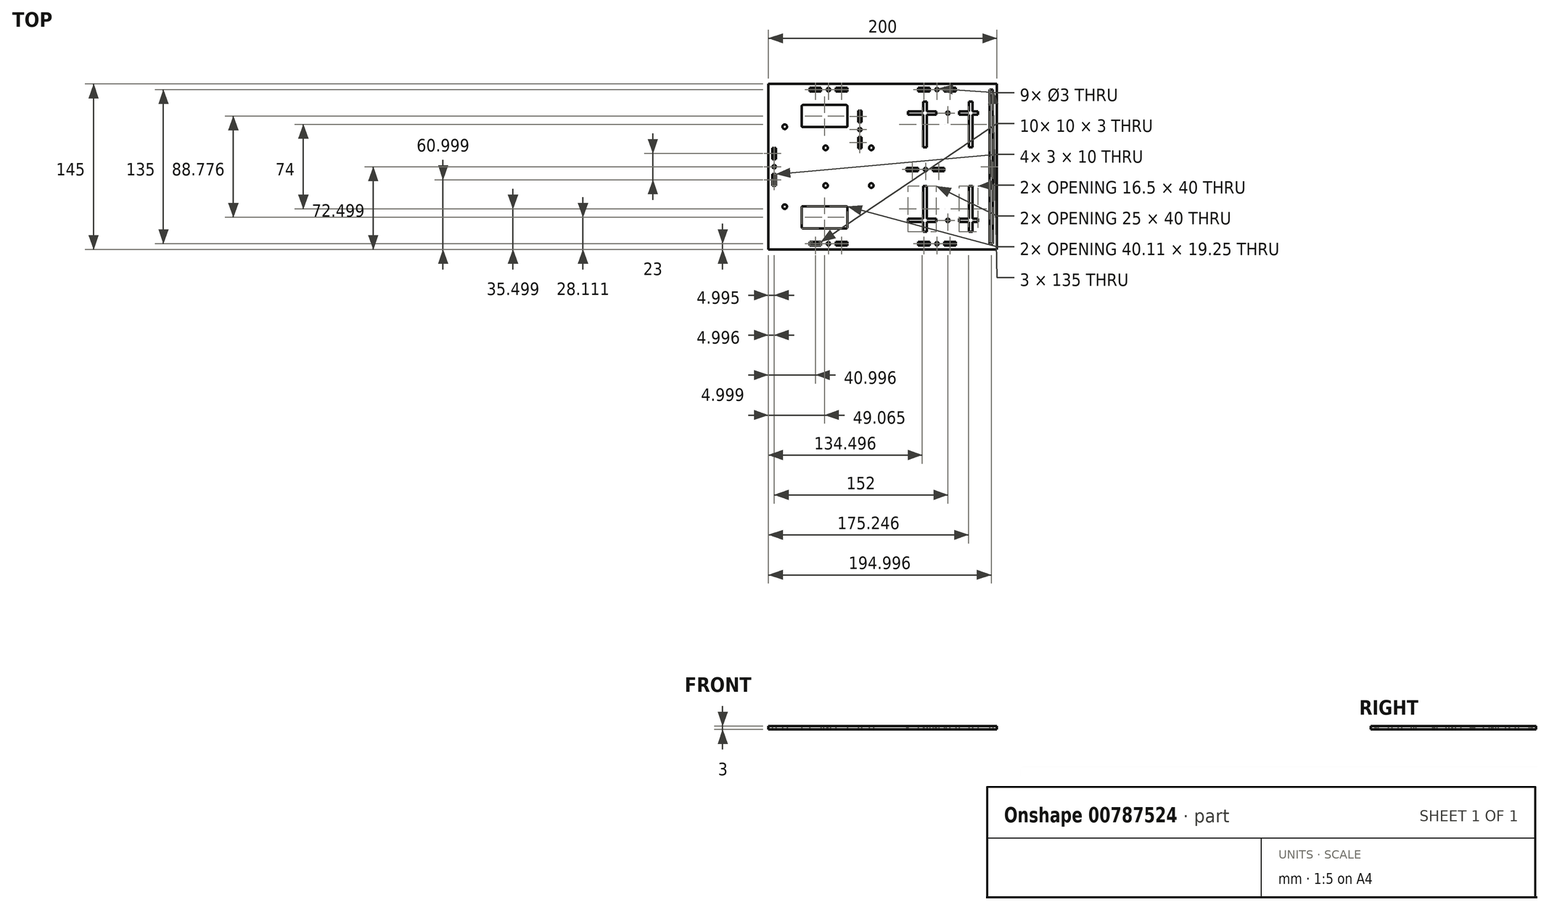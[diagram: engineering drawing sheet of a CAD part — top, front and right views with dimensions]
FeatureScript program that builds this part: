
annotation { "Feature Type Name" : "Feature", "Feature Type Description" : "" }
export const myFeature = defineFeature(function(context is Context, id is Id, definition is map)
    precondition{}
    {
        {
            var Q0;
            Q0=qCreatedBy(makeId("Top.planeOp"),FACE);
            var sketch = newSketch(context, id + "F0", { "sketchPlane" : qUnion([Q0])});
            skLineSegment(sketch, "E0.bottom", {"start": v(-57.36, 121.67) * mm, "end": v(142.64, 121.67) * mm});
            skLineSegment(sketch, "E0.top", {"start": v(-57.36, -23.33) * mm, "end": v(142.64, -23.33) * mm});
            skLineSegment(sketch, "E0.left", {"start": v(-57.36, 121.67) * mm, "end": v(-57.36, -23.33) * mm});
            skLineSegment(sketch, "E0.right", {"start": v(142.64, 121.67) * mm, "end": v(142.64, -23.33) * mm});
            skLineSegment(sketch, "E1.top", {"start": v(137.64, 46.67) * mm, "end": v(22.64, 46.67) * mm, "construction": true});
            skLineSegment(sketch, "E1.right", {"start": v(22.64, 116.67) * mm, "end": v(22.64, 46.67) * mm, "construction": true});
            skLineSegment(sketch, "E2", {"start": v(-57.36, 49.17) * mm, "end": v(-42.36, 49.17) * mm, "construction": true});
            skLineSegment(sketch, "E3.0", {"start": v(137.64, 116.67) * mm, "end": v(137.64, -18.33) * mm, "construction": true});
            skLineSegment(sketch, "E4.bottom", {"start": v(136.14, 116.67) * mm, "end": v(139.14, 116.67) * mm});
            skLineSegment(sketch, "E4.top", {"start": v(136.14, -18.33) * mm, "end": v(139.14, -18.33) * mm});
            skLineSegment(sketch, "E4.left", {"start": v(136.14, 116.67) * mm, "end": v(136.14, -18.33) * mm});
            skLineSegment(sketch, "E4.right", {"start": v(139.14, 116.67) * mm, "end": v(139.14, -18.33) * mm});
            skPoint(sketch, "E4.middle", {"position": v(137.64, 49.17) * mm});
            skLineSegment(sketch, "E5.0", {"start": v(-52.36, 116.67) * mm, "end": v(146, 116.67) * mm, "construction": true});
            skLineSegment(sketch, "E6.0", {"start": v(-52.36, 116.67) * mm, "end": v(-52.36, -18.33) * mm, "construction": true});
            skLineSegment(sketch, "E7.0", {"start": v(-52.36, -18.33) * mm, "end": v(139.14, -18.33) * mm, "construction": true});
            skCircle(sketch, "E8", {"center": v(90.14, 116.67) * mm, "radius": 1.5 * mm});
            skCircle(sketch, "E9", {"center": v(-4.86, 116.67) * mm, "radius": 1.5 * mm});
            skPoint(sketch, "E10", {"position": v(-52.36, 116.67) * mm});
            skLineSegment(sketch, "E11.bottom", {"start": v(-21.36, 118.17) * mm, "end": v(-11.36, 118.17) * mm});
            skLineSegment(sketch, "E11.top", {"start": v(-21.36, 115.17) * mm, "end": v(-11.36, 115.17) * mm});
            skLineSegment(sketch, "E11.left", {"start": v(-21.36, 118.17) * mm, "end": v(-21.36, 115.17) * mm});
            skLineSegment(sketch, "E11.right", {"start": v(-11.36, 118.17) * mm, "end": v(-11.36, 115.17) * mm});
            skPoint(sketch, "E11.middle", {"position": v(-16.36, 116.67) * mm});
            skLineSegment(sketch, "E12.bottom", {"start": v(1.64, 118.17) * mm, "end": v(11.64, 118.17) * mm});
            skLineSegment(sketch, "E12.top", {"start": v(1.64, 115.17) * mm, "end": v(11.64, 115.17) * mm});
            skLineSegment(sketch, "E12.left", {"start": v(1.64, 118.17) * mm, "end": v(1.64, 115.17) * mm});
            skLineSegment(sketch, "E12.right", {"start": v(11.64, 118.17) * mm, "end": v(11.64, 115.17) * mm});
            skPoint(sketch, "E12.middle", {"position": v(6.64, 116.67) * mm});
            skLineSegment(sketch, "E13.bottom", {"start": v(73.64, 118.17) * mm, "end": v(83.64, 118.17) * mm});
            skLineSegment(sketch, "E13.top", {"start": v(73.64, 115.17) * mm, "end": v(83.64, 115.17) * mm});
            skLineSegment(sketch, "E13.left", {"start": v(73.64, 118.17) * mm, "end": v(73.64, 115.17) * mm});
            skLineSegment(sketch, "E13.right", {"start": v(83.64, 118.17) * mm, "end": v(83.64, 115.17) * mm});
            skPoint(sketch, "E13.middle", {"position": v(78.64, 116.67) * mm});
            skLineSegment(sketch, "E14.bottom", {"start": v(96.64, 118.17) * mm, "end": v(106.64, 118.17) * mm});
            skLineSegment(sketch, "E14.top", {"start": v(96.64, 115.17) * mm, "end": v(106.64, 115.17) * mm});
            skLineSegment(sketch, "E14.left", {"start": v(96.64, 118.17) * mm, "end": v(96.64, 115.17) * mm});
            skLineSegment(sketch, "E14.right", {"start": v(106.64, 118.17) * mm, "end": v(106.64, 115.17) * mm});
            skPoint(sketch, "E14.middle", {"position": v(101.64, 116.67) * mm});
            skLineSegment(sketch, "E15.MirrorCS", {"start": v(11.64, -19.83) * mm, "end": v(11.64, -16.83) * mm});
            skLineSegment(sketch, "E16.MirrorCS", {"start": v(-21.36, -19.83) * mm, "end": v(-11.36, -19.83) * mm});
            skLineSegment(sketch, "E17.MirrorCS", {"start": v(-21.36, -16.83) * mm, "end": v(-11.36, -16.83) * mm});
            skLineSegment(sketch, "E18.MirrorCS", {"start": v(1.64, -19.83) * mm, "end": v(11.64, -19.83) * mm});
            skLineSegment(sketch, "E19.MirrorCS", {"start": v(-21.36, -19.83) * mm, "end": v(-21.36, -16.83) * mm});
            skLineSegment(sketch, "E20.MirrorCS", {"start": v(1.64, -16.83) * mm, "end": v(11.64, -16.83) * mm});
            skCircle(sketch, "E21.MirrorC", {"center": v(-4.86, -18.33) * mm, "radius": 1.5 * mm});
            skPoint(sketch, "E22.MirrorP", {"position": v(-16.36, -18.33) * mm});
            skLineSegment(sketch, "E23.MirrorCS", {"start": v(-11.36, -19.83) * mm, "end": v(-11.36, -16.83) * mm});
            skLineSegment(sketch, "E24.MirrorCS", {"start": v(1.64, -19.83) * mm, "end": v(1.64, -16.83) * mm});
            skPoint(sketch, "E25.MirrorP", {"position": v(6.64, -18.33) * mm});
            skLineSegment(sketch, "E26.MirrorCS", {"start": v(106.64, -19.83) * mm, "end": v(106.64, -16.83) * mm});
            skLineSegment(sketch, "E27.MirrorCS", {"start": v(83.64, -19.83) * mm, "end": v(83.64, -16.83) * mm});
            skLineSegment(sketch, "E28.MirrorCS", {"start": v(96.64, -19.83) * mm, "end": v(96.64, -16.83) * mm});
            skLineSegment(sketch, "E29.MirrorCS", {"start": v(73.64, -19.83) * mm, "end": v(73.64, -16.83) * mm});
            skPoint(sketch, "E30.MirrorP", {"position": v(101.64, -18.33) * mm});
            skCircle(sketch, "E31.MirrorC", {"center": v(90.14, -18.33) * mm, "radius": 1.5 * mm});
            skLineSegment(sketch, "E32.MirrorCS", {"start": v(73.64, -16.83) * mm, "end": v(83.64, -16.83) * mm});
            skLineSegment(sketch, "E33.MirrorCS", {"start": v(96.64, -16.83) * mm, "end": v(106.64, -16.83) * mm});
            skPoint(sketch, "E34.MirrorP", {"position": v(78.64, -18.33) * mm});
            skLineSegment(sketch, "E35.MirrorCS", {"start": v(73.64, -19.83) * mm, "end": v(83.64, -19.83) * mm});
            skLineSegment(sketch, "E36.MirrorCS", {"start": v(96.64, -19.83) * mm, "end": v(106.64, -19.83) * mm});
            skLineSegment(sketch, "E37.0.1.0", {"start": v(24.13, 98.17) * mm, "end": v(24.13, 88.17) * mm});
            skLineSegment(sketch, "E37.0.1.1", {"start": v(21.13, 98.17) * mm, "end": v(24.13, 98.17) * mm});
            skLineSegment(sketch, "E37.0.1.2", {"start": v(21.13, 98.17) * mm, "end": v(21.13, 88.17) * mm});
            skLineSegment(sketch, "E37.0.1.3", {"start": v(21.13, 88.17) * mm, "end": v(24.13, 88.17) * mm});
            skCircle(sketch, "E37.0.1.4", {"center": v(22.64, 81.67) * mm, "radius": 1.5 * mm});
            skLineSegment(sketch, "E37.0.1.5", {"start": v(21.13, 75.17) * mm, "end": v(24.13, 75.17) * mm});
            skLineSegment(sketch, "E37.0.1.6", {"start": v(24.13, 75.17) * mm, "end": v(24.13, 65.17) * mm});
            skLineSegment(sketch, "E37.0.1.7", {"start": v(21.13, 65.17) * mm, "end": v(24.13, 65.17) * mm});
            skLineSegment(sketch, "E37.0.1.8", {"start": v(21.13, 75.17) * mm, "end": v(21.13, 65.17) * mm});
            skLineSegment(sketch, "E37.0.2.0", {"start": v(63.64, 48.17) * mm, "end": v(73.64, 48.17) * mm});
            skLineSegment(sketch, "E37.0.2.1", {"start": v(63.64, 45.17) * mm, "end": v(63.64, 48.17) * mm});
            skLineSegment(sketch, "E37.0.2.2", {"start": v(63.64, 45.17) * mm, "end": v(73.64, 45.17) * mm});
            skLineSegment(sketch, "E37.0.2.3", {"start": v(73.64, 45.17) * mm, "end": v(73.64, 48.17) * mm});
            skCircle(sketch, "E37.0.2.4", {"center": v(80.14, 46.67) * mm, "radius": 1.5 * mm});
            skLineSegment(sketch, "E37.0.2.5", {"start": v(86.64, 45.17) * mm, "end": v(86.64, 48.17) * mm});
            skLineSegment(sketch, "E37.0.2.6", {"start": v(86.64, 48.17) * mm, "end": v(96.64, 48.17) * mm});
            skLineSegment(sketch, "E37.0.2.7", {"start": v(96.64, 45.17) * mm, "end": v(96.64, 48.17) * mm});
            skLineSegment(sketch, "E37.0.2.8", {"start": v(86.64, 45.17) * mm, "end": v(96.64, 45.17) * mm});
            skLineSegment(sketch, "E38.0.1.0", {"start": v(-50.87, 65.67) * mm, "end": v(-50.87, 55.67) * mm});
            skLineSegment(sketch, "E38.0.1.1", {"start": v(-53.87, 65.67) * mm, "end": v(-50.87, 65.67) * mm});
            skLineSegment(sketch, "E38.0.1.2", {"start": v(-53.87, 65.67) * mm, "end": v(-53.87, 55.67) * mm});
            skLineSegment(sketch, "E38.0.1.3", {"start": v(-53.87, 55.67) * mm, "end": v(-50.87, 55.67) * mm});
            skCircle(sketch, "E38.0.1.4", {"center": v(-52.36, 49.17) * mm, "radius": 1.5 * mm});
            skLineSegment(sketch, "E38.0.1.5", {"start": v(-53.87, 42.67) * mm, "end": v(-50.87, 42.67) * mm});
            skLineSegment(sketch, "E38.0.1.6", {"start": v(-50.87, 42.67) * mm, "end": v(-50.87, 32.67) * mm});
            skLineSegment(sketch, "E38.0.1.7", {"start": v(-53.87, 32.67) * mm, "end": v(-50.87, 32.67) * mm});
            skLineSegment(sketch, "E38.0.1.8", {"start": v(-53.87, 42.67) * mm, "end": v(-53.87, 32.67) * mm});
            skLineSegment(sketch, "E39.0", {"start": v(-57.36, 84.17) * mm, "end": v(-43.11, 84.17) * mm, "construction": true});
            skCircle(sketch, "E40", {"center": v(-43.11, 84.17) * mm, "radius": 2 * mm});
            skCircle(sketch, "E41.MirrorC", {"center": v(-43.11, 14.17) * mm, "radius": 2 * mm});
            skLineSegment(sketch, "E42.bottom", {"start": v(-27.35, 14.4) * mm, "end": v(10.76, 14.4) * mm});
            skLineSegment(sketch, "E42.top", {"start": v(-27.35, -4.85) * mm, "end": v(10.76, -4.85) * mm});
            skLineSegment(sketch, "E42.left", {"start": v(-28.35, 13.4) * mm, "end": v(-28.35, -3.85) * mm});
            skLineSegment(sketch, "E42.right", {"start": v(11.76, 13.4) * mm, "end": v(11.76, -3.85) * mm});
            skPoint(sketch, "E43.visualSharp", {"position": v(-28.35, 14.4) * mm});
            skArc(sketch, "E43.filletArc", {"start": v(-27.35, 14.4) * mm, "mid": v(-28.05, 14.12) * mm, "end": v(-28.35, 13.4) * mm});
            skPoint(sketch, "E44.visualSharp", {"position": v(11.76, 14.4) * mm});
            skArc(sketch, "E44.filletArc", {"start": v(11.76, 13.4) * mm, "mid": v(11.47, 14.12) * mm, "end": v(10.76, 14.4) * mm});
            skPoint(sketch, "E45.visualSharp", {"position": v(11.76, -4.85) * mm});
            skArc(sketch, "E45.filletArc", {"start": v(10.76, -4.85) * mm, "mid": v(11.47, -4.55) * mm, "end": v(11.76, -3.85) * mm});
            skPoint(sketch, "E46.visualSharp", {"position": v(-28.35, -4.85) * mm});
            skArc(sketch, "E46.filletArc", {"start": v(-28.35, -3.85) * mm, "mid": v(-28.05, -4.55) * mm, "end": v(-27.35, -4.85) * mm});
            skLineSegment(sketch, "E47.bottom", {"start": v(118.14, 32.17) * mm, "end": v(121.14, 32.17) * mm});
            skLineSegment(sketch, "E47.top", {"start": v(118.14, -7.83) * mm, "end": v(121.14, -7.83) * mm});
            skLineSegment(sketch, "E47.left", {"start": v(118.14, 32.17) * mm, "end": v(118.14, -7.83) * mm});
            skLineSegment(sketch, "E47.right", {"start": v(121.14, 32.17) * mm, "end": v(121.14, -7.83) * mm});
            skPoint(sketch, "E47.middle", {"position": v(119.64, 12.17) * mm});
            skLineSegment(sketch, "E48.bottom", {"start": v(109.64, 3.67) * mm, "end": v(126.14, 3.67) * mm});
            skLineSegment(sketch, "E48.top", {"start": v(109.64, 0.67) * mm, "end": v(126.14, 0.67) * mm});
            skLineSegment(sketch, "E48.left", {"start": v(109.64, 3.67) * mm, "end": v(109.64, 0.67) * mm});
            skLineSegment(sketch, "E48.right", {"start": v(126.14, 3.67) * mm, "end": v(126.14, 0.67) * mm});
            skPoint(sketch, "E48.middle", {"position": v(117.89, 2.17) * mm});
            skLineSegment(sketch, "E49.bottom", {"start": v(81.14, 32.17) * mm, "end": v(78.14, 32.17) * mm});
            skLineSegment(sketch, "E49.top", {"start": v(81.14, -7.83) * mm, "end": v(78.14, -7.83) * mm});
            skLineSegment(sketch, "E49.left", {"start": v(81.14, 32.17) * mm, "end": v(81.14, -7.83) * mm});
            skLineSegment(sketch, "E49.right", {"start": v(78.14, 32.17) * mm, "end": v(78.14, -7.83) * mm});
            skPoint(sketch, "E49.middle", {"position": v(79.64, 12.17) * mm});
            skLineSegment(sketch, "E50.bottom", {"start": v(89.64, 3.67) * mm, "end": v(64.64, 3.67) * mm});
            skLineSegment(sketch, "E50.top", {"start": v(89.64, 0.67) * mm, "end": v(64.64, 0.67) * mm});
            skLineSegment(sketch, "E50.left", {"start": v(89.64, 3.67) * mm, "end": v(89.64, 0.67) * mm});
            skLineSegment(sketch, "E50.right", {"start": v(64.64, 3.67) * mm, "end": v(64.64, 0.67) * mm});
            skPoint(sketch, "E50.middle", {"position": v(77.14, 2.17) * mm});
            skLineSegment(sketch, "E51.MirrorCS", {"start": v(118.14, 106.17) * mm, "end": v(121.14, 106.17) * mm});
            skLineSegment(sketch, "E52.MirrorCS", {"start": v(81.14, 66.17) * mm, "end": v(78.14, 66.17) * mm});
            skLineSegment(sketch, "E53.MirrorCS", {"start": v(89.64, 94.67) * mm, "end": v(89.64, 97.67) * mm});
            skLineSegment(sketch, "E54.MirrorCS", {"start": v(81.14, 106.17) * mm, "end": v(78.14, 106.17) * mm});
            skLineSegment(sketch, "E55.MirrorCS", {"start": v(64.64, 94.67) * mm, "end": v(64.64, 97.67) * mm});
            skLineSegment(sketch, "E56.MirrorCS", {"start": v(118.14, 66.17) * mm, "end": v(121.14, 66.17) * mm});
            skLineSegment(sketch, "E57.MirrorCS", {"start": v(126.14, 94.67) * mm, "end": v(126.14, 97.67) * mm});
            skLineSegment(sketch, "E58.MirrorCS", {"start": v(109.64, 94.67) * mm, "end": v(109.64, 97.67) * mm});
            skLineSegment(sketch, "E59.MirrorCS", {"start": v(109.64, 97.67) * mm, "end": v(126.14, 97.67) * mm});
            skLineSegment(sketch, "E60.MirrorCS", {"start": v(109.64, 94.67) * mm, "end": v(126.14, 94.67) * mm});
            skPoint(sketch, "E61.MirrorP", {"position": v(79.64, 86.17) * mm});
            skPoint(sketch, "E62.MirrorP", {"position": v(77.14, 96.17) * mm});
            skLineSegment(sketch, "E63.MirrorCS", {"start": v(78.14, 66.17) * mm, "end": v(78.14, 106.17) * mm});
            skLineSegment(sketch, "E64.MirrorCS", {"start": v(81.14, 66.17) * mm, "end": v(81.14, 106.17) * mm});
            skLineSegment(sketch, "E65.MirrorCS", {"start": v(89.64, 97.67) * mm, "end": v(64.64, 97.67) * mm});
            skLineSegment(sketch, "E66.MirrorCS", {"start": v(121.14, 66.17) * mm, "end": v(121.14, 106.17) * mm});
            skLineSegment(sketch, "E67.MirrorCS", {"start": v(89.64, 94.67) * mm, "end": v(64.64, 94.67) * mm});
            skLineSegment(sketch, "E68.MirrorCS", {"start": v(118.14, 66.17) * mm, "end": v(118.14, 106.17) * mm});
            skPoint(sketch, "E69.MirrorP", {"position": v(119.64, 86.17) * mm});
            skPoint(sketch, "E70.MirrorP", {"position": v(117.89, 96.17) * mm});
            skPoint(sketch, "E71", {"position": v(142.64, 49.17) * mm});
            skLineSegment(sketch, "E72", {"start": v(89.64, 96.17) * mm, "end": v(109.64, 96.17) * mm, "construction": true});
            skCircle(sketch, "E73", {"center": v(99.64, 96.17) * mm, "radius": 1.5 * mm});
            skLineSegment(sketch, "E74", {"start": v(89.64, 2.17) * mm, "end": v(109.64, 2.17) * mm, "construction": true});
            skCircle(sketch, "E75", {"center": v(99.64, 2.17) * mm, "radius": 1.5 * mm});
            skArc(sketch, "E76.MirrorCS", {"start": v(10.76, 103.18) * mm, "mid": v(11.47, 102.9) * mm, "end": v(11.76, 102.18) * mm});
            skArc(sketch, "E77.MirrorCS", {"start": v(-27.35, 83.93) * mm, "mid": v(-28.05, 84.22) * mm, "end": v(-28.35, 84.93) * mm});
            skArc(sketch, "E78.MirrorCS", {"start": v(-28.35, 102.18) * mm, "mid": v(-28.05, 102.9) * mm, "end": v(-27.35, 103.18) * mm});
            skArc(sketch, "E79.MirrorCS", {"start": v(11.76, 84.93) * mm, "mid": v(11.47, 84.22) * mm, "end": v(10.76, 83.93) * mm});
            skLineSegment(sketch, "E80.MirrorCS", {"start": v(-28.35, 84.93) * mm, "end": v(-28.35, 102.18) * mm});
            skLineSegment(sketch, "E81.MirrorCS", {"start": v(-27.35, 83.93) * mm, "end": v(10.76, 83.93) * mm});
            skLineSegment(sketch, "E82.MirrorCS", {"start": v(11.76, 84.93) * mm, "end": v(11.76, 102.18) * mm});
            skLineSegment(sketch, "E83.MirrorCS", {"start": v(-27.35, 103.18) * mm, "end": v(10.76, 103.18) * mm});
            skPoint(sketch, "E84.MirrorP", {"position": v(-28.35, 103.18) * mm});
            skPoint(sketch, "E85.MirrorP", {"position": v(-28.35, 83.93) * mm});
            skPoint(sketch, "E86.MirrorP", {"position": v(11.76, 83.93) * mm});
            skPoint(sketch, "E87.MirrorP", {"position": v(11.76, 103.18) * mm});
            skLineSegment(sketch, "E88.bottom", {"start": v(130.63, 287) * mm, "end": v(239.77, 287) * mm});
            skLineSegment(sketch, "E88.top", {"start": v(130.63, 162) * mm, "end": v(239.77, 162) * mm});
            skLineSegment(sketch, "E88.left", {"start": v(130.63, 287) * mm, "end": v(130.63, 162) * mm});
            skLineSegment(sketch, "E88.right", {"start": v(239.77, 287) * mm, "end": v(239.77, 162) * mm});
            skLineSegment(sketch, "E89", {"start": v(-42.36, 49.17) * mm, "end": v(13.94, 49.17) * mm, "construction": true});
            skCircle(sketch, "E90", {"center": v(32.64, 65.67) * mm, "radius": 2 * mm});
            skCircle(sketch, "E91", {"center": v(-7.36, 65.67) * mm, "radius": 2 * mm});
            skCircle(sketch, "E92.MirrorC", {"center": v(32.64, 32.67) * mm, "radius": 2 * mm});
            skCircle(sketch, "E93.MirrorC", {"center": v(-7.36, 32.67) * mm, "radius": 2 * mm});
            skSolve(sketch);
        }
        {
            var Q0;
            Q0=makeQuery(id+"F0.imprint","IMPRINT",FACE,{"disambiguationData":[TD([[makeQuery(id+"F0.imprint","IMPRINT",EDGE,{"derivedFrom":sQuery(id+"F0.wireOp",EDGE,"E0.bottom")}),-1.0]])]});
            extrude(context, id + "F1", {"entities" : qUnion([Q0]), "depth" : 3 * mm, "offsetDistance" : 25.4 * mm});
        }
    });
